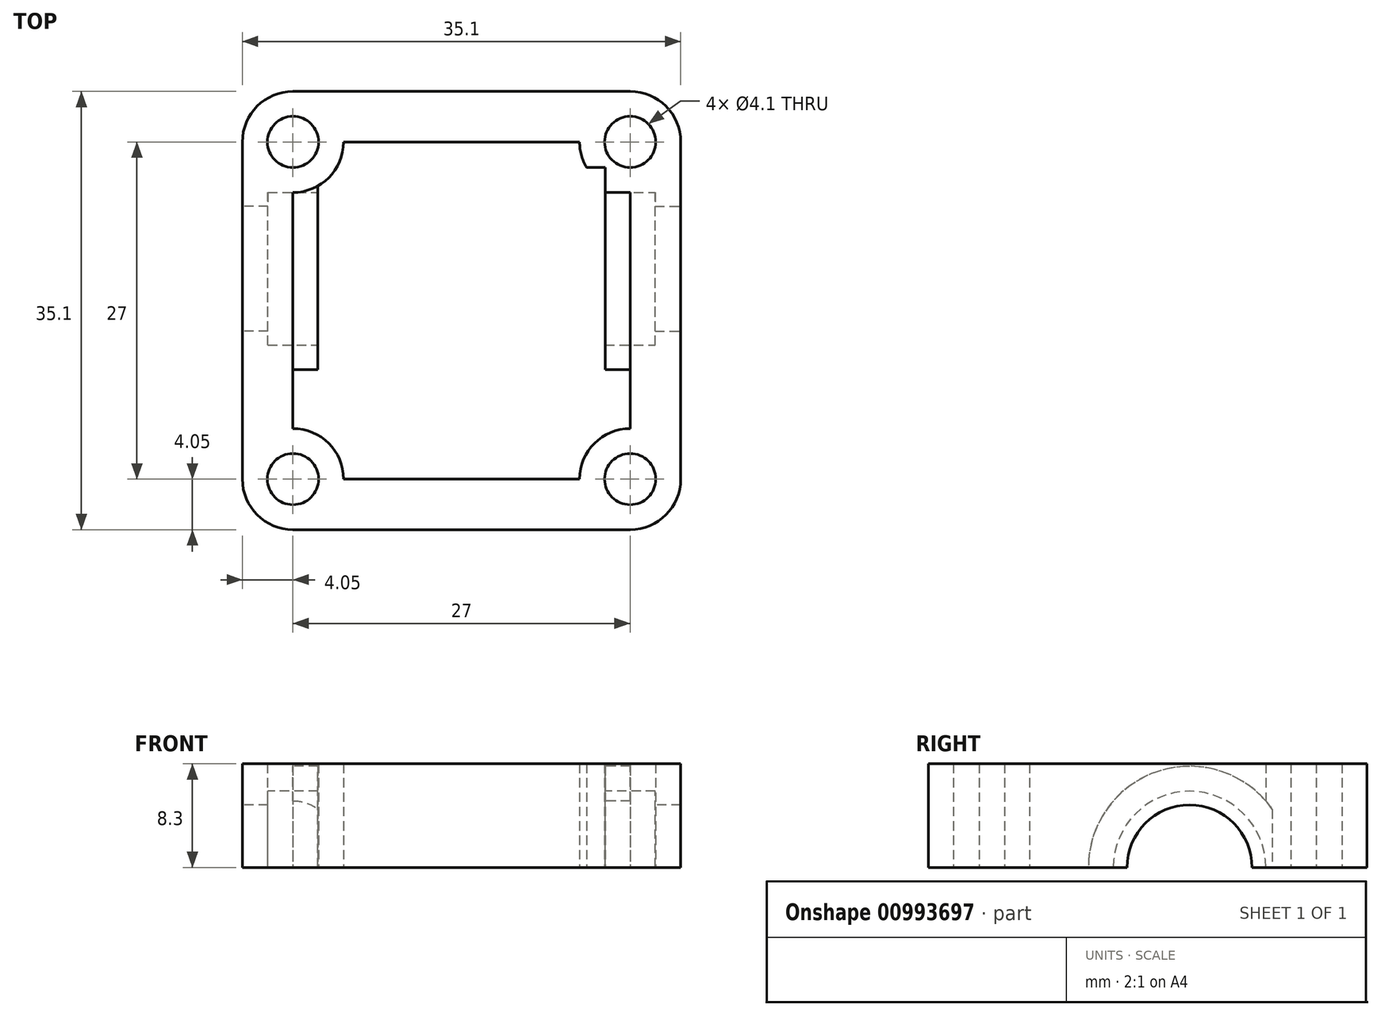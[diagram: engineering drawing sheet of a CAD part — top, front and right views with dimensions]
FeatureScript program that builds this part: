
annotation { "Feature Type Name" : "Feature", "Feature Type Description" : "" }
export const myFeature = defineFeature(function(context is Context, id is Id, definition is map)
    precondition{}
    {
        {
            var Q0;
            Q0=qCreatedBy(makeId("Top.planeOp"),FACE);
            var sketch = newSketch(context, id + "F0", { "sketchPlane" : qUnion([Q0])});
            skLineSegment(sketch, "E0.bottom", {"start": v(17.55, 17.55) * mm, "end": v(-17.55, 17.55) * mm});
            skLineSegment(sketch, "E0.top", {"start": v(17.55, -17.55) * mm, "end": v(-17.55, -17.55) * mm});
            skLineSegment(sketch, "E0.left", {"start": v(17.55, 17.55) * mm, "end": v(17.55, -17.55) * mm});
            skLineSegment(sketch, "E0.right", {"start": v(-17.55, 17.55) * mm, "end": v(-17.55, -17.55) * mm});
            skPoint(sketch, "E0.middle", {"position": v(0, 0) * mm});
            skLineSegment(sketch, "E1", {"start": v(0, 0) * mm, "end": v(0, 17.55) * mm, "construction": true});
            skLineSegment(sketch, "E2", {"start": v(0, 0) * mm, "end": v(-17.55, 0) * mm, "construction": true});
            skLineSegment(sketch, "E3.bottom", {"start": v(13.5, 13.5) * mm, "end": v(-13.5, 13.5) * mm});
            skLineSegment(sketch, "E3.top", {"start": v(13.5, -13.5) * mm, "end": v(-13.5, -13.5) * mm});
            skLineSegment(sketch, "E3.left", {"start": v(13.5, 13.5) * mm, "end": v(13.5, -13.5) * mm});
            skLineSegment(sketch, "E3.right", {"start": v(-13.5, 13.5) * mm, "end": v(-13.5, -13.5) * mm});
            skCircle(sketch, "E4", {"center": v(-13.5, 13.5) * mm, "radius": 2.05 * mm});
            skCircle(sketch, "E5", {"center": v(-13.5, 13.5) * mm, "radius": 4.05 * mm});
            skCircle(sketch, "E6.MirrorC", {"center": v(13.5, 13.5) * mm, "radius": 4.05 * mm});
            skCircle(sketch, "E7.MirrorC", {"center": v(13.5, 13.5) * mm, "radius": 2.05 * mm});
            skCircle(sketch, "E8.MirrorC", {"center": v(-13.5, -13.5) * mm, "radius": 4.05 * mm});
            skCircle(sketch, "E9.MirrorC", {"center": v(-13.5, -13.5) * mm, "radius": 2.05 * mm});
            skCircle(sketch, "E10.MirrorC", {"center": v(13.5, -13.5) * mm, "radius": 4.05 * mm});
            skCircle(sketch, "E11.MirrorC", {"center": v(13.5, -13.5) * mm, "radius": 2.05 * mm});
            skLineSegment(sketch, "E12", {"start": v(-15.5, 11.45) * mm, "end": v(15.5, 11.45) * mm});
            skLineSegment(sketch, "E13", {"start": v(15.5, 11.45) * mm, "end": v(15.5, -4.75) * mm});
            skLineSegment(sketch, "E14", {"start": v(15.5, -4.75) * mm, "end": v(-15.5, -4.75) * mm});
            skLineSegment(sketch, "E15", {"start": v(-15.5, 11.45) * mm, "end": v(-15.5, -4.75) * mm});
            skLineSegment(sketch, "E16", {"start": v(-15.5, 3.35) * mm, "end": v(15.5, 3.35) * mm});
            skLineSegment(sketch, "E17", {"start": v(15.5, -2.75) * mm, "end": v(-15.5, -2.75) * mm});
            skLineSegment(sketch, "E18", {"start": v(-15.5, 9.45) * mm, "end": v(15.5, 9.45) * mm});
            skLineSegment(sketch, "E19", {"start": v(-11.5, 11.45) * mm, "end": v(-11.5, -4.75) * mm});
            skLineSegment(sketch, "E20", {"start": v(11.5, 11.45) * mm, "end": v(11.5, -4.75) * mm});
            skLineSegment(sketch, "E21", {"start": v(-15.5, 3.35) * mm, "end": v(-17.55, 3.35) * mm});
            skLineSegment(sketch, "E22", {"start": v(15.5, 3.35) * mm, "end": v(17.55, 3.35) * mm});
            skLineSegment(sketch, "E23", {"start": v(-15.5, 8.35) * mm, "end": v(-17.55, 8.35) * mm});
            skLineSegment(sketch, "E24", {"start": v(15.5, 8.35) * mm, "end": v(17.55, 8.35) * mm});
            skSolve(sketch);
        }
        {
            var Q0;
            {var subQ0=sQuery(id+"F0.wireOp",EDGE,"E15");var subQ3=sQuery(id+"F0.wireOp",EDGE,"E18");var subQ5=makeQuery(id+"F0.imprint","INTERSECT",VERTEX,{"derivedFrom":[subQ0,subQ3]});Q0=makeQuery(id+"F0.imprint","IMPRINT",FACE,{"disambiguationData":[TD([[makeQuery(id+"F0.imprint","IMPRINT",EDGE,{"disambiguationData":[TD([[subQ5,1.0]])],"derivedFrom":subQ0}),1.0]])]});}
            var Q1;
            {var subQ0=sQuery(id+"F0.wireOp",EDGE,"E5");var subQ3=sQuery(id+"F0.wireOp",EDGE,"E3.bottom");var subQ4=makeQuery(id+"F0.imprint","INTERSECT",VERTEX,{"derivedFrom":[subQ3,subQ0]});Q1=makeQuery(id+"F0.imprint","IMPRINT",FACE,{"disambiguationData":[TD([[makeQuery(id+"F0.imprint","IMPRINT",EDGE,{"disambiguationData":[TD([[subQ4,-1.0]])],"derivedFrom":subQ3}),-1.0]])]});}
            var Q2;
            {var subQ0=sQuery(id+"F0.wireOp",EDGE,"E12");var subQ5=sQuery(id+"F0.wireOp",EDGE,"E15");var subQ7=makeQuery(id+"F0.imprint","INTERSECT",VERTEX,{"derivedFrom":[subQ0,subQ5]});Q2=makeQuery(id+"F0.imprint","IMPRINT",FACE,{"disambiguationData":[TD([[makeQuery(id+"F0.imprint","IMPRINT",EDGE,{"disambiguationData":[TD([[subQ7,-1.0]])],"derivedFrom":subQ5}),1.0]])]});}
            var Q3;
            {var subQ1=sQuery(id+"F0.wireOp",EDGE,"E0.right");var subQ7=sQuery(id+"F0.wireOp",EDGE,"E5");var subQ8=makeQuery(id+"F0.imprint","INTERSECT",VERTEX,{"derivedFrom":[subQ1,subQ7]});Q3=makeQuery(id+"F0.imprint","IMPRINT",FACE,{"disambiguationData":[TD([[makeQuery(id+"F0.imprint","IMPRINT",EDGE,{"disambiguationData":[TD([[subQ8,-1.0]])],"derivedFrom":subQ1}),1.0]])]});}
            var Q4;
            {var subQ0=sQuery(id+"F0.wireOp",EDGE,"E17");var subQ5=sQuery(id+"F0.wireOp",EDGE,"E15");var subQ7=makeQuery(id+"F0.imprint","INTERSECT",VERTEX,{"derivedFrom":[subQ5,subQ0]});Q4=makeQuery(id+"F0.imprint","IMPRINT",FACE,{"disambiguationData":[TD([[makeQuery(id+"F0.imprint","IMPRINT",EDGE,{"disambiguationData":[TD([[subQ7,1.0]])],"derivedFrom":subQ5}),1.0]])]});}
            var Q5;
            {var subQ0=sQuery(id+"F0.wireOp",EDGE,"E17");var subQ1=sQuery(id+"F0.wireOp",EDGE,"E3.right");var subQ2=makeQuery(id+"F0.imprint","INTERSECT",VERTEX,{"derivedFrom":[subQ1,subQ0]});Q5=makeQuery(id+"F0.imprint","IMPRINT",FACE,{"disambiguationData":[TD([[makeQuery(id+"F0.imprint","IMPRINT",EDGE,{"disambiguationData":[TD([[subQ2,-1.0]])],"derivedFrom":subQ1}),-1.0]])]});}
            var Q6;
            {var subQ0=sQuery(id+"F0.wireOp",EDGE,"E8.MirrorC");var subQ2=sQuery(id+"F0.wireOp",EDGE,"E3.top");var subQ3=makeQuery(id+"F0.imprint","INTERSECT",VERTEX,{"derivedFrom":[subQ2,subQ0]});Q6=makeQuery(id+"F0.imprint","IMPRINT",FACE,{"disambiguationData":[TD([[makeQuery(id+"F0.imprint","IMPRINT",EDGE,{"disambiguationData":[TD([[subQ3,-1.0]])],"derivedFrom":subQ2}),1.0]])]});}
            var Q7;
            {var subQ0=sQuery(id+"F0.wireOp",EDGE,"E10.MirrorC");var subQ1=sQuery(id+"F0.wireOp",EDGE,"E0.top");var subQ2=makeQuery(id+"F0.imprint","INTERSECT",VERTEX,{"derivedFrom":[subQ1,subQ0]});Q7=makeQuery(id+"F0.imprint","IMPRINT",FACE,{"disambiguationData":[TD([[makeQuery(id+"F0.imprint","IMPRINT",EDGE,{"disambiguationData":[TD([[subQ2,-1.0]])],"derivedFrom":subQ1}),-1.0]])]});}
            var Q8;
            {var subQ0=sQuery(id+"F0.wireOp",EDGE,"E8.MirrorC");var subQ1=sQuery(id+"F0.wireOp",EDGE,"E3.top");var subQ2=makeQuery(id+"F0.imprint","INTERSECT",VERTEX,{"derivedFrom":[subQ1,subQ0]});Q8=makeQuery(id+"F0.imprint","IMPRINT",FACE,{"disambiguationData":[TD([[makeQuery(id+"F0.imprint","IMPRINT",EDGE,{"disambiguationData":[TD([[subQ2,-1.0]])],"derivedFrom":subQ1}),-1.0]])]});}
            var Q9;
            {var subQ3=sQuery(id+"F0.wireOp",EDGE,"E3.top");var subQ7=sQuery(id+"F0.wireOp",EDGE,"E11.MirrorC");var subQ9=makeQuery(id+"F0.imprint","INTERSECT",VERTEX,{"derivedFrom":[subQ3,subQ7]});Q9=makeQuery(id+"F0.imprint","IMPRINT",FACE,{"disambiguationData":[TD([[makeQuery(id+"F0.imprint","IMPRINT",EDGE,{"disambiguationData":[TD([[subQ9,-1.0]])],"derivedFrom":subQ3}),1.0]])]});}
            var Q10;
            {var subQ0=sQuery(id+"F0.wireOp",EDGE,"E11.MirrorC");var subQ1=sQuery(id+"F0.wireOp",EDGE,"E3.top");var subQ2=makeQuery(id+"F0.imprint","INTERSECT",VERTEX,{"derivedFrom":[subQ1,subQ0]});Q10=makeQuery(id+"F0.imprint","IMPRINT",FACE,{"disambiguationData":[TD([[makeQuery(id+"F0.imprint","IMPRINT",EDGE,{"disambiguationData":[TD([[subQ2,-1.0]])],"derivedFrom":subQ1}),-1.0]])]});}
            var Q11;
            {var subQ5=sQuery(id+"F0.wireOp",EDGE,"E0.left");var subQ7=sQuery(id+"F0.wireOp",EDGE,"E6.MirrorC");var subQ8=makeQuery(id+"F0.imprint","INTERSECT",VERTEX,{"derivedFrom":[subQ5,subQ7]});Q11=makeQuery(id+"F0.imprint","IMPRINT",FACE,{"disambiguationData":[TD([[makeQuery(id+"F0.imprint","IMPRINT",EDGE,{"disambiguationData":[TD([[subQ8,-1.0]])],"derivedFrom":subQ5}),-1.0]])]});}
            var Q12;
            {var subQ0=sQuery(id+"F0.wireOp",EDGE,"E17");var subQ1=sQuery(id+"F0.wireOp",EDGE,"E3.left");var subQ2=makeQuery(id+"F0.imprint","INTERSECT",VERTEX,{"derivedFrom":[subQ1,subQ0]});Q12=makeQuery(id+"F0.imprint","IMPRINT",FACE,{"disambiguationData":[TD([[makeQuery(id+"F0.imprint","IMPRINT",EDGE,{"disambiguationData":[TD([[subQ2,-1.0]])],"derivedFrom":subQ1}),1.0]])]});}
            var Q13;
            {var subQ0=sQuery(id+"F0.wireOp",EDGE,"E17");var subQ5=sQuery(id+"F0.wireOp",EDGE,"E13");var subQ6=makeQuery(id+"F0.imprint","INTERSECT",VERTEX,{"derivedFrom":[subQ5,subQ0]});Q13=makeQuery(id+"F0.imprint","IMPRINT",FACE,{"disambiguationData":[TD([[makeQuery(id+"F0.imprint","IMPRINT",EDGE,{"disambiguationData":[TD([[subQ6,1.0]])],"derivedFrom":subQ5}),-1.0]])]});}
            var Q14;
            {var subQ0=sQuery(id+"F0.wireOp",EDGE,"E13");var subQ3=sQuery(id+"F0.wireOp",EDGE,"E18");var subQ5=makeQuery(id+"F0.imprint","INTERSECT",VERTEX,{"derivedFrom":[subQ0,subQ3]});Q14=makeQuery(id+"F0.imprint","IMPRINT",FACE,{"disambiguationData":[TD([[makeQuery(id+"F0.imprint","IMPRINT",EDGE,{"disambiguationData":[TD([[subQ5,1.0]])],"derivedFrom":subQ0}),-1.0]])]});}
            var Q15;
            {var subQ0=sQuery(id+"F0.wireOp",EDGE,"E12");var subQ5=sQuery(id+"F0.wireOp",EDGE,"E13");var subQ7=makeQuery(id+"F0.imprint","INTERSECT",VERTEX,{"derivedFrom":[subQ0,subQ5]});Q15=makeQuery(id+"F0.imprint","IMPRINT",FACE,{"disambiguationData":[TD([[makeQuery(id+"F0.imprint","IMPRINT",EDGE,{"disambiguationData":[TD([[subQ7,-1.0]])],"derivedFrom":subQ5}),-1.0]])]});}
            var Q16;
            {var subQ0=sQuery(id+"F0.wireOp",EDGE,"E12");var subQ5=sQuery(id+"F0.wireOp",EDGE,"E20");var subQ7=makeQuery(id+"F0.imprint","INTERSECT",VERTEX,{"derivedFrom":[subQ0,subQ5]});Q16=makeQuery(id+"F0.imprint","IMPRINT",FACE,{"disambiguationData":[TD([[makeQuery(id+"F0.imprint","IMPRINT",EDGE,{"disambiguationData":[TD([[subQ7,-1.0]])],"derivedFrom":subQ5}),1.0]])]});}
            var Q17;
            {var subQ0=sQuery(id+"F0.wireOp",EDGE,"E20");var subQ1=sQuery(id+"F0.wireOp",EDGE,"E6.MirrorC");var subQ2=makeQuery(id+"F0.imprint","INTERSECT",VERTEX,{"derivedFrom":[subQ1,subQ0]});Q17=makeQuery(id+"F0.imprint","IMPRINT",FACE,{"disambiguationData":[TD([[makeQuery(id+"F0.imprint","IMPRINT",EDGE,{"disambiguationData":[TD([[subQ2,-1.0]])],"derivedFrom":subQ1}),-1.0]])]});}
            var Q18;
            {var subQ4=sQuery(id+"F0.wireOp",EDGE,"E3.bottom");var subQ6=sQuery(id+"F0.wireOp",EDGE,"E7.MirrorC");var subQ7=makeQuery(id+"F0.imprint","INTERSECT",VERTEX,{"derivedFrom":[subQ4,subQ6]});Q18=makeQuery(id+"F0.imprint","IMPRINT",FACE,{"disambiguationData":[TD([[makeQuery(id+"F0.imprint","IMPRINT",EDGE,{"disambiguationData":[TD([[subQ7,-1.0]])],"derivedFrom":subQ4}),1.0]])]});}
            var Q19;
            {var subQ5=sQuery(id+"F0.wireOp",EDGE,"E7.MirrorC");var subQ6=sQuery(id+"F0.wireOp",EDGE,"E3.bottom");var subQ7=makeQuery(id+"F0.imprint","INTERSECT",VERTEX,{"derivedFrom":[subQ6,subQ5]});Q19=makeQuery(id+"F0.imprint","IMPRINT",FACE,{"disambiguationData":[TD([[makeQuery(id+"F0.imprint","IMPRINT",EDGE,{"disambiguationData":[TD([[subQ7,-1.0]])],"derivedFrom":subQ6}),-1.0]])]});}
            var Q20;
            {var subQ0=sQuery(id+"F0.wireOp",EDGE,"E6.MirrorC");var subQ1=sQuery(id+"F0.wireOp",EDGE,"E0.bottom");var subQ2=makeQuery(id+"F0.imprint","INTERSECT",VERTEX,{"derivedFrom":[subQ1,subQ0]});Q20=makeQuery(id+"F0.imprint","IMPRINT",FACE,{"disambiguationData":[TD([[makeQuery(id+"F0.imprint","IMPRINT",EDGE,{"disambiguationData":[TD([[subQ2,-1.0]])],"derivedFrom":subQ1}),1.0]])]});}
            var Q21;
            {var subQ0=sQuery(id+"F0.wireOp",EDGE,"E5");var subQ1=sQuery(id+"F0.wireOp",EDGE,"E3.bottom");var subQ2=makeQuery(id+"F0.imprint","INTERSECT",VERTEX,{"derivedFrom":[subQ1,subQ0]});Q21=makeQuery(id+"F0.imprint","IMPRINT",FACE,{"disambiguationData":[TD([[makeQuery(id+"F0.imprint","IMPRINT",EDGE,{"disambiguationData":[TD([[subQ2,-1.0]])],"derivedFrom":subQ1}),1.0]])]});}
            var Q22;
            {var subQ0=sQuery(id+"F0.wireOp",EDGE,"E12");var subQ5=sQuery(id+"F0.wireOp",EDGE,"E19");var subQ7=makeQuery(id+"F0.imprint","INTERSECT",VERTEX,{"derivedFrom":[subQ0,subQ5]});Q22=makeQuery(id+"F0.imprint","IMPRINT",FACE,{"disambiguationData":[TD([[makeQuery(id+"F0.imprint","IMPRINT",EDGE,{"disambiguationData":[TD([[subQ7,-1.0]])],"derivedFrom":subQ5}),-1.0]])]});}
            var Q23;
            {var subQ0=sQuery(id+"F0.wireOp",EDGE,"E19");var subQ1=sQuery(id+"F0.wireOp",EDGE,"E5");var subQ2=makeQuery(id+"F0.imprint","INTERSECT",VERTEX,{"derivedFrom":[subQ1,subQ0]});Q23=makeQuery(id+"F0.imprint","IMPRINT",FACE,{"disambiguationData":[TD([[makeQuery(id+"F0.imprint","IMPRINT",EDGE,{"disambiguationData":[TD([[subQ2,-1.0]])],"derivedFrom":subQ1}),1.0]])]});}
            var Q24;
            {var subQ10=sQuery(id+"F0.wireOp",EDGE,"E21");Q24=makeQuery(id+"F0.imprint","IMPRINT",FACE,{"disambiguationData":[TD([[makeQuery(id+"F0.imprint","IMPRINT",EDGE,{"derivedFrom":subQ10}),1.0]])]});}
            var Q25;
            {var subQ0=sQuery(id+"F0.wireOp",EDGE,"E21");Q25=makeQuery(id+"F0.imprint","IMPRINT",FACE,{"disambiguationData":[TD([[makeQuery(id+"F0.imprint","IMPRINT",EDGE,{"derivedFrom":subQ0}),-1.0]])]});}
            var Q26;
            {var subQ1=sQuery(id+"F0.wireOp",EDGE,"E15");var subQ4=sQuery(id+"F0.wireOp",EDGE,"E18");var subQ5=makeQuery(id+"F0.imprint","INTERSECT",VERTEX,{"derivedFrom":[subQ1,subQ4]});Q26=makeQuery(id+"F0.imprint","IMPRINT",FACE,{"disambiguationData":[TD([[makeQuery(id+"F0.imprint","IMPRINT",EDGE,{"disambiguationData":[TD([[subQ5,-1.0]])],"derivedFrom":subQ1}),1.0]])]});}
            var Q27;
            {var subQ0=sQuery(id+"F0.wireOp",EDGE,"E22");Q27=makeQuery(id+"F0.imprint","IMPRINT",FACE,{"disambiguationData":[TD([[makeQuery(id+"F0.imprint","IMPRINT",EDGE,{"derivedFrom":subQ0}),1.0]])]});}
            var Q28;
            {var subQ1=sQuery(id+"F0.wireOp",EDGE,"E13");var subQ6=sQuery(id+"F0.wireOp",EDGE,"E18");var subQ7=makeQuery(id+"F0.imprint","INTERSECT",VERTEX,{"derivedFrom":[subQ1,subQ6]});Q28=makeQuery(id+"F0.imprint","IMPRINT",FACE,{"disambiguationData":[TD([[makeQuery(id+"F0.imprint","IMPRINT",EDGE,{"disambiguationData":[TD([[subQ7,-1.0]])],"derivedFrom":subQ1}),-1.0]])]});}
            var Q29;
            {var subQ0=sQuery(id+"F0.wireOp",EDGE,"E22");Q29=makeQuery(id+"F0.imprint","IMPRINT",FACE,{"disambiguationData":[TD([[makeQuery(id+"F0.imprint","IMPRINT",EDGE,{"derivedFrom":subQ0}),-1.0]])]});}
            var Q30;
            {var subQ0=sQuery(id+"F0.wireOp",EDGE,"E18");var subQ1=sQuery(id+"F0.wireOp",EDGE,"E6.MirrorC");var subQ2=makeQuery(id+"F0.imprint","INTERSECT",VERTEX,{"derivedFrom":[subQ1,subQ0]});Q30=makeQuery(id+"F0.imprint","IMPRINT",FACE,{"disambiguationData":[TD([[makeQuery(id+"F0.imprint","IMPRINT",EDGE,{"disambiguationData":[TD([[subQ2,-1.0]])],"derivedFrom":subQ1}),-1.0]])]});}
            var Q31;
            {var subQ0=sQuery(id+"F0.wireOp",EDGE,"E18");var subQ1=sQuery(id+"F0.wireOp",EDGE,"E5");var subQ2=makeQuery(id+"F0.imprint","INTERSECT",VERTEX,{"derivedFrom":[subQ1,subQ0]});Q31=makeQuery(id+"F0.imprint","IMPRINT",FACE,{"disambiguationData":[TD([[makeQuery(id+"F0.imprint","IMPRINT",EDGE,{"disambiguationData":[TD([[subQ2,-1.0]])],"derivedFrom":subQ1}),1.0]])]});}
            var Q32;
            {var subQ4=sQuery(id+"F0.wireOp",EDGE,"E5");var subQ6=sQuery(id+"F0.wireOp",EDGE,"E3.right");var subQ7=makeQuery(id+"F0.imprint","INTERSECT",VERTEX,{"derivedFrom":[subQ6,subQ4]});Q32=makeQuery(id+"F0.imprint","IMPRINT",FACE,{"disambiguationData":[TD([[makeQuery(id+"F0.imprint","IMPRINT",EDGE,{"disambiguationData":[TD([[subQ7,-1.0]])],"derivedFrom":subQ6}),-1.0]])]});}
            var Q33;
            {var subQ4=sQuery(id+"F0.wireOp",EDGE,"E6.MirrorC");var subQ6=sQuery(id+"F0.wireOp",EDGE,"E3.left");var subQ7=makeQuery(id+"F0.imprint","INTERSECT",VERTEX,{"derivedFrom":[subQ6,subQ4]});Q33=makeQuery(id+"F0.imprint","IMPRINT",FACE,{"disambiguationData":[TD([[makeQuery(id+"F0.imprint","IMPRINT",EDGE,{"disambiguationData":[TD([[subQ7,-1.0]])],"derivedFrom":subQ6}),1.0]])]});}
            extrude(context, id + "F1", {"entities" : qUnion([Q0, Q1, Q2, Q3, Q4, Q5, Q6, Q7, Q8, Q9, Q10, Q11, Q12, Q13, Q14, Q15, Q16, Q17, Q18, Q19, Q20, Q21, Q22, Q23, Q24, Q25, Q26, Q27, Q28, Q29, Q30, Q31, Q32, Q33]), "depth" : (((12 + 0.6 + 2 * 2) / 2)) * mm, "offsetDistance" : 25 * mm});
        }
        {
            var Q0;
            {var subQ0=sQuery(id+"F0.wireOp",EDGE,"E21");Q0=makeQuery(id+"F0.imprint","IMPRINT",FACE,{"disambiguationData":[TD([[makeQuery(id+"F0.imprint","IMPRINT",EDGE,{"derivedFrom":subQ0}),-1.0]])]});}
            var Q1;
            {var subQ1=sQuery(id+"F0.wireOp",EDGE,"E15");var subQ4=sQuery(id+"F0.wireOp",EDGE,"E18");var subQ5=makeQuery(id+"F0.imprint","INTERSECT",VERTEX,{"derivedFrom":[subQ1,subQ4]});Q1=makeQuery(id+"F0.imprint","IMPRINT",FACE,{"disambiguationData":[TD([[makeQuery(id+"F0.imprint","IMPRINT",EDGE,{"disambiguationData":[TD([[subQ5,-1.0]])],"derivedFrom":subQ1}),1.0]])]});}
            var Q2;
            {var subQ0=sQuery(id+"F0.wireOp",EDGE,"E16");var subQ1=sQuery(id+"F0.wireOp",EDGE,"E3.right");var subQ2=makeQuery(id+"F0.imprint","INTERSECT",VERTEX,{"derivedFrom":[subQ1,subQ0]});Q2=makeQuery(id+"F0.imprint","IMPRINT",FACE,{"disambiguationData":[TD([[makeQuery(id+"F0.imprint","IMPRINT",EDGE,{"disambiguationData":[TD([[subQ2,-1.0]])],"derivedFrom":subQ0}),1.0]])]});}
            var Q3;
            {var subQ0=sQuery(id+"F0.wireOp",EDGE,"E12");var subQ5=sQuery(id+"F0.wireOp",EDGE,"E19");var subQ7=makeQuery(id+"F0.imprint","INTERSECT",VERTEX,{"derivedFrom":[subQ0,subQ5]});Q3=makeQuery(id+"F0.imprint","IMPRINT",FACE,{"disambiguationData":[TD([[makeQuery(id+"F0.imprint","IMPRINT",EDGE,{"disambiguationData":[TD([[subQ7,-1.0]])],"derivedFrom":subQ5}),-1.0]])]});}
            var Q4;
            {var subQ0=sQuery(id+"F0.wireOp",EDGE,"E12");var subQ5=sQuery(id+"F0.wireOp",EDGE,"E15");var subQ6=makeQuery(id+"F0.imprint","INTERSECT",VERTEX,{"derivedFrom":[subQ0,subQ5]});Q4=makeQuery(id+"F0.imprint","IMPRINT",FACE,{"disambiguationData":[TD([[makeQuery(id+"F0.imprint","IMPRINT",EDGE,{"disambiguationData":[TD([[subQ6,-1.0]])],"derivedFrom":subQ5}),1.0]])]});}
            var Q5;
            {var subQ0=sQuery(id+"F0.wireOp",EDGE,"E12");var subQ5=sQuery(id+"F0.wireOp",EDGE,"E20");var subQ6=makeQuery(id+"F0.imprint","INTERSECT",VERTEX,{"derivedFrom":[subQ0,subQ5]});Q5=makeQuery(id+"F0.imprint","IMPRINT",FACE,{"disambiguationData":[TD([[makeQuery(id+"F0.imprint","IMPRINT",EDGE,{"disambiguationData":[TD([[subQ6,-1.0]])],"derivedFrom":subQ5}),1.0]])]});}
            var Q6;
            {var subQ0=sQuery(id+"F0.wireOp",EDGE,"E16");var subQ1=sQuery(id+"F0.wireOp",EDGE,"E3.left");var subQ2=makeQuery(id+"F0.imprint","INTERSECT",VERTEX,{"derivedFrom":[subQ1,subQ0]});Q6=makeQuery(id+"F0.imprint","IMPRINT",FACE,{"disambiguationData":[TD([[makeQuery(id+"F0.imprint","IMPRINT",EDGE,{"disambiguationData":[TD([[subQ2,1.0]])],"derivedFrom":subQ0}),1.0]])]});}
            var Q7;
            {var subQ0=sQuery(id+"F0.wireOp",EDGE,"E12");var subQ5=sQuery(id+"F0.wireOp",EDGE,"E13");var subQ7=makeQuery(id+"F0.imprint","INTERSECT",VERTEX,{"derivedFrom":[subQ0,subQ5]});Q7=makeQuery(id+"F0.imprint","IMPRINT",FACE,{"disambiguationData":[TD([[makeQuery(id+"F0.imprint","IMPRINT",EDGE,{"disambiguationData":[TD([[subQ7,-1.0]])],"derivedFrom":subQ5}),-1.0]])]});}
            var Q8;
            {var subQ0=sQuery(id+"F0.wireOp",EDGE,"E19");var subQ1=sQuery(id+"F0.wireOp",EDGE,"E5");var subQ2=makeQuery(id+"F0.imprint","INTERSECT",VERTEX,{"derivedFrom":[subQ1,subQ0]});Q8=makeQuery(id+"F0.imprint","IMPRINT",FACE,{"disambiguationData":[TD([[makeQuery(id+"F0.imprint","IMPRINT",EDGE,{"disambiguationData":[TD([[subQ2,-1.0]])],"derivedFrom":subQ0}),-1.0]])]});}
            var Q9;
            {var subQ0=sQuery(id+"F0.wireOp",EDGE,"E15");var subQ3=sQuery(id+"F0.wireOp",EDGE,"E18");var subQ5=makeQuery(id+"F0.imprint","INTERSECT",VERTEX,{"derivedFrom":[subQ0,subQ3]});Q9=makeQuery(id+"F0.imprint","IMPRINT",FACE,{"disambiguationData":[TD([[makeQuery(id+"F0.imprint","IMPRINT",EDGE,{"disambiguationData":[TD([[subQ5,1.0]])],"derivedFrom":subQ0}),1.0]])]});}
            var Q10;
            {var subQ0=sQuery(id+"F0.wireOp",EDGE,"E13");var subQ3=sQuery(id+"F0.wireOp",EDGE,"E18");var subQ5=makeQuery(id+"F0.imprint","INTERSECT",VERTEX,{"derivedFrom":[subQ0,subQ3]});Q10=makeQuery(id+"F0.imprint","IMPRINT",FACE,{"disambiguationData":[TD([[makeQuery(id+"F0.imprint","IMPRINT",EDGE,{"disambiguationData":[TD([[subQ5,1.0]])],"derivedFrom":subQ0}),-1.0]])]});}
            var Q11;
            {var subQ0=sQuery(id+"F0.wireOp",EDGE,"E20");var subQ1=sQuery(id+"F0.wireOp",EDGE,"E6.MirrorC");var subQ2=makeQuery(id+"F0.imprint","INTERSECT",VERTEX,{"derivedFrom":[subQ1,subQ0]});Q11=makeQuery(id+"F0.imprint","IMPRINT",FACE,{"disambiguationData":[TD([[makeQuery(id+"F0.imprint","IMPRINT",EDGE,{"disambiguationData":[TD([[subQ2,-1.0]])],"derivedFrom":subQ0}),1.0]])]});}
            var Q12;
            {var subQ0=sQuery(id+"F0.wireOp",EDGE,"E18");var subQ1=sQuery(id+"F0.wireOp",EDGE,"E3.left");var subQ2=makeQuery(id+"F0.imprint","INTERSECT",VERTEX,{"derivedFrom":[subQ1,subQ0]});Q12=makeQuery(id+"F0.imprint","IMPRINT",FACE,{"disambiguationData":[TD([[makeQuery(id+"F0.imprint","IMPRINT",EDGE,{"disambiguationData":[TD([[subQ2,-1.0]])],"derivedFrom":subQ1}),-1.0]])]});}
            var Q13;
            {var subQ0=sQuery(id+"F0.wireOp",EDGE,"E22");Q13=makeQuery(id+"F0.imprint","IMPRINT",FACE,{"disambiguationData":[TD([[makeQuery(id+"F0.imprint","IMPRINT",EDGE,{"derivedFrom":subQ0}),1.0]])]});}
            var Q14;
            {var subQ4=sQuery(id+"F0.wireOp",EDGE,"E6.MirrorC");var subQ6=sQuery(id+"F0.wireOp",EDGE,"E3.left");var subQ7=makeQuery(id+"F0.imprint","INTERSECT",VERTEX,{"derivedFrom":[subQ6,subQ4]});Q14=makeQuery(id+"F0.imprint","IMPRINT",FACE,{"disambiguationData":[TD([[makeQuery(id+"F0.imprint","IMPRINT",EDGE,{"disambiguationData":[TD([[subQ7,-1.0]])],"derivedFrom":subQ6}),1.0]])]});}
            var Q15;
            {var subQ0=sQuery(id+"F0.wireOp",EDGE,"E18");var subQ1=sQuery(id+"F0.wireOp",EDGE,"E3.left");var subQ2=makeQuery(id+"F0.imprint","INTERSECT",VERTEX,{"derivedFrom":[subQ1,subQ0]});Q15=makeQuery(id+"F0.imprint","IMPRINT",FACE,{"disambiguationData":[TD([[makeQuery(id+"F0.imprint","IMPRINT",EDGE,{"disambiguationData":[TD([[subQ2,-1.0]])],"derivedFrom":subQ1}),1.0]])]});}
            var Q16;
            {var subQ0=sQuery(id+"F0.wireOp",EDGE,"E18");var subQ1=sQuery(id+"F0.wireOp",EDGE,"E3.right");var subQ2=makeQuery(id+"F0.imprint","INTERSECT",VERTEX,{"derivedFrom":[subQ1,subQ0]});Q16=makeQuery(id+"F0.imprint","IMPRINT",FACE,{"disambiguationData":[TD([[makeQuery(id+"F0.imprint","IMPRINT",EDGE,{"disambiguationData":[TD([[subQ2,-1.0]])],"derivedFrom":subQ1}),1.0]])]});}
            var Q17;
            Q17=sQuery(id+"F0.wireOp",EDGE,"E16");
            revolve(context, id + "F2", {"operationType" : NewBodyOperationType.ADD, "surfaceOperationType" : NewSurfaceOperationType.NEW, "entities" : qUnion([Q0, Q1, Q2, Q3, Q4, Q5, Q6, Q7, Q8, Q9, Q10, Q11, Q12, Q13, Q14, Q15, Q16]), "axis" : qUnion([Q17]), "revolveType" : RevolveType.ONE_DIRECTION, "angle" : 180 * degree});
        }
        {
            var Q0;
            {var subQ1=sQuery(id+"F0.wireOp",EDGE,"E13");var subQ6=sQuery(id+"F0.wireOp",EDGE,"E18");var subQ7=makeQuery(id+"F0.imprint","INTERSECT",VERTEX,{"derivedFrom":[subQ1,subQ6]});Q0=makeQuery(id+"F0.imprint","IMPRINT",FACE,{"disambiguationData":[TD([[makeQuery(id+"F0.imprint","IMPRINT",EDGE,{"disambiguationData":[TD([[subQ7,-1.0]])],"derivedFrom":subQ1}),-1.0]])]});}
            var Q1;
            {var subQ0=sQuery(id+"F0.wireOp",EDGE,"E22");Q1=makeQuery(id+"F0.imprint","IMPRINT",FACE,{"disambiguationData":[TD([[makeQuery(id+"F0.imprint","IMPRINT",EDGE,{"derivedFrom":subQ0}),1.0]])]});}
            var Q2;
            {var subQ0=sQuery(id+"F0.wireOp",EDGE,"E16");var subQ1=sQuery(id+"F0.wireOp",EDGE,"E3.left");var subQ2=makeQuery(id+"F0.imprint","INTERSECT",VERTEX,{"derivedFrom":[subQ1,subQ0]});Q2=makeQuery(id+"F0.imprint","IMPRINT",FACE,{"disambiguationData":[TD([[makeQuery(id+"F0.imprint","IMPRINT",EDGE,{"disambiguationData":[TD([[subQ2,1.0]])],"derivedFrom":subQ0}),1.0]])]});}
            var Q3;
            {var subQ0=sQuery(id+"F0.wireOp",EDGE,"E16");var subQ1=sQuery(id+"F0.wireOp",EDGE,"E3.right");var subQ2=makeQuery(id+"F0.imprint","INTERSECT",VERTEX,{"derivedFrom":[subQ1,subQ0]});Q3=makeQuery(id+"F0.imprint","IMPRINT",FACE,{"disambiguationData":[TD([[makeQuery(id+"F0.imprint","IMPRINT",EDGE,{"disambiguationData":[TD([[subQ2,-1.0]])],"derivedFrom":subQ0}),1.0]])]});}
            var Q4;
            {var subQ1=sQuery(id+"F0.wireOp",EDGE,"E15");var subQ4=sQuery(id+"F0.wireOp",EDGE,"E18");var subQ5=makeQuery(id+"F0.imprint","INTERSECT",VERTEX,{"derivedFrom":[subQ1,subQ4]});Q4=makeQuery(id+"F0.imprint","IMPRINT",FACE,{"disambiguationData":[TD([[makeQuery(id+"F0.imprint","IMPRINT",EDGE,{"disambiguationData":[TD([[subQ5,-1.0]])],"derivedFrom":subQ1}),1.0]])]});}
            var Q5;
            {var subQ0=sQuery(id+"F0.wireOp",EDGE,"E21");Q5=makeQuery(id+"F0.imprint","IMPRINT",FACE,{"disambiguationData":[TD([[makeQuery(id+"F0.imprint","IMPRINT",EDGE,{"derivedFrom":subQ0}),-1.0]])]});}
            var Q6;
            {var subQ4=sQuery(id+"F0.wireOp",EDGE,"E5");var subQ6=sQuery(id+"F0.wireOp",EDGE,"E3.right");var subQ7=makeQuery(id+"F0.imprint","INTERSECT",VERTEX,{"derivedFrom":[subQ6,subQ4]});Q6=makeQuery(id+"F0.imprint","IMPRINT",FACE,{"disambiguationData":[TD([[makeQuery(id+"F0.imprint","IMPRINT",EDGE,{"disambiguationData":[TD([[subQ7,-1.0]])],"derivedFrom":subQ6}),-1.0]])]});}
            var Q7;
            {var subQ4=sQuery(id+"F0.wireOp",EDGE,"E6.MirrorC");var subQ6=sQuery(id+"F0.wireOp",EDGE,"E3.left");var subQ7=makeQuery(id+"F0.imprint","INTERSECT",VERTEX,{"derivedFrom":[subQ6,subQ4]});Q7=makeQuery(id+"F0.imprint","IMPRINT",FACE,{"disambiguationData":[TD([[makeQuery(id+"F0.imprint","IMPRINT",EDGE,{"disambiguationData":[TD([[subQ7,-1.0]])],"derivedFrom":subQ6}),1.0]])]});}
            var Q8;
            {var subQ0=sQuery(id+"F0.wireOp",EDGE,"E18");var subQ1=sQuery(id+"F0.wireOp",EDGE,"E3.right");var subQ2=makeQuery(id+"F0.imprint","INTERSECT",VERTEX,{"derivedFrom":[subQ1,subQ0]});Q8=makeQuery(id+"F0.imprint","IMPRINT",FACE,{"disambiguationData":[TD([[makeQuery(id+"F0.imprint","IMPRINT",EDGE,{"disambiguationData":[TD([[subQ2,-1.0]])],"derivedFrom":subQ1}),1.0]])]});}
            var Q9;
            {var subQ0=sQuery(id+"F0.wireOp",EDGE,"E18");var subQ1=sQuery(id+"F0.wireOp",EDGE,"E3.left");var subQ2=makeQuery(id+"F0.imprint","INTERSECT",VERTEX,{"derivedFrom":[subQ1,subQ0]});Q9=makeQuery(id+"F0.imprint","IMPRINT",FACE,{"disambiguationData":[TD([[makeQuery(id+"F0.imprint","IMPRINT",EDGE,{"disambiguationData":[TD([[subQ2,-1.0]])],"derivedFrom":subQ1}),-1.0]])]});}
            var Q10;
            Q10=sQuery(id+"F0.wireOp",EDGE,"E16");
            revolve(context, id + "F3", {"operationType" : NewBodyOperationType.REMOVE, "surfaceOperationType" : NewSurfaceOperationType.NEW, "entities" : qUnion([Q0, Q1, Q2, Q3, Q4, Q5, Q6, Q7, Q8, Q9]), "axis" : qUnion([Q10]), "revolveType" : RevolveType.ONE_DIRECTION, "angle" : 180 * degree});
        }
    });
